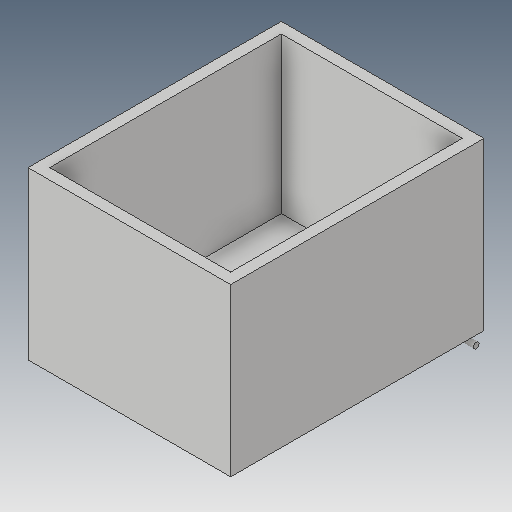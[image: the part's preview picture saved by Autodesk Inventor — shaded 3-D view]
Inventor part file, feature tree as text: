
AUTODESK INVENTOR PART (.ipt)
format: ipt  version: 2019 (Build 230136000, 136)  size: 111,616 bytes
history: native  units: mm
features: extrude x2, sketch x2
ambient origin geometry x8: Origin, YZ Plane, XZ Plane, XY Plane, X Axis, Y Axis, Z Axis, Center Point
bodies: Body1 (feature_tree)
feature tree (4):
  extrude  "돌출2"  Depth=460.0mm
  extrude  "돌출3"  Depth=700.0mm
  sketch  "스케치1"
  sketch  "스케치2"
